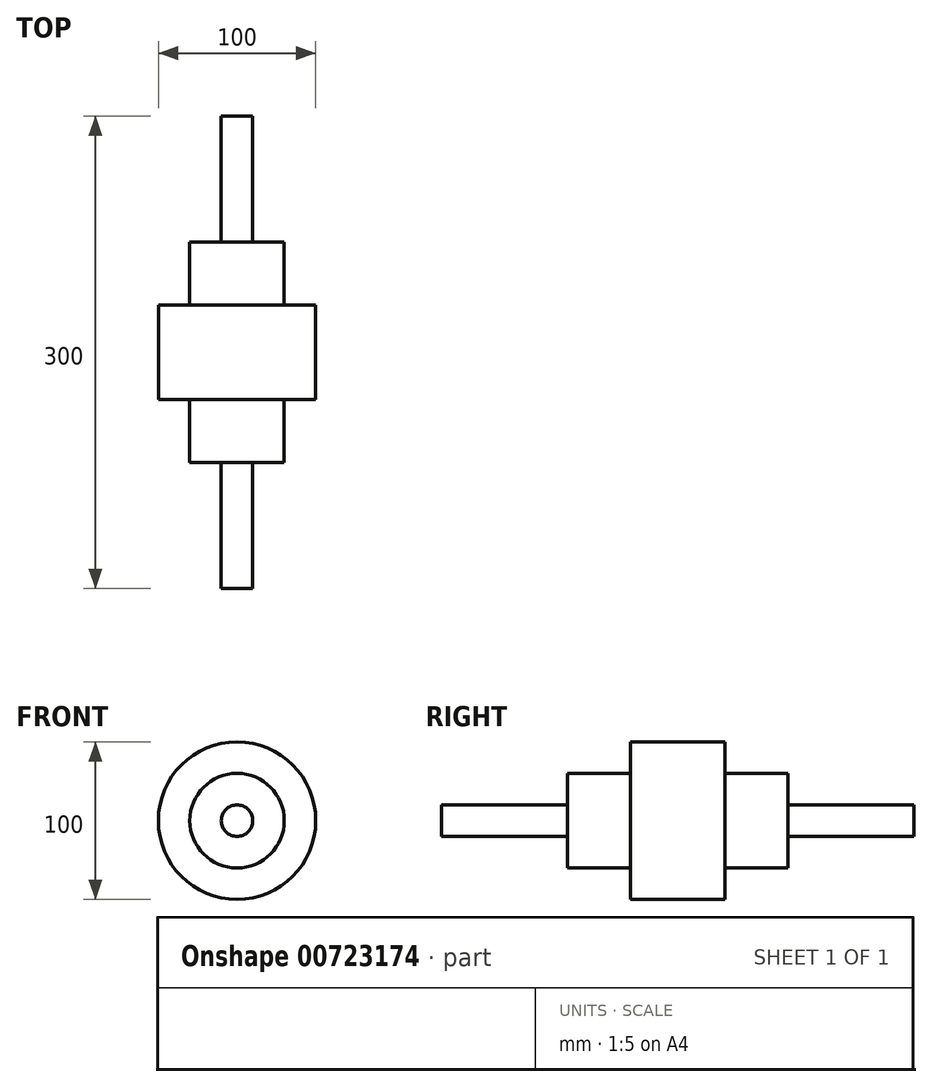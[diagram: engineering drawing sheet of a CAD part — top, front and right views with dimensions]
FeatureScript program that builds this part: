
annotation { "Feature Type Name" : "Feature", "Feature Type Description" : "" }
export const myFeature = defineFeature(function(context is Context, id is Id, definition is map)
    precondition{}
    {
        {
            var Q0;
            Q0=qCreatedBy(makeId("Front.planeOp"),FACE);
            var sketch = newSketch(context, id + "F0", { "sketchPlane" : qUnion([Q0])});
            skCircle(sketch, "E0", {"center": v(0, 0) * mm, "radius": 50 * mm});
            skSolve(sketch);
        }
        {
            var Q0;
            Q0 = qSketchRegion(id + "F0", true);
            extrude(context, id + "F1", {"entities" : qUnion([Q0]), "depth" : 60 * mm, "offsetDistance" : 25.4 * mm});
        }
        {
            var Q0;
            Q0=makeQuery(id+"F1.opExtrude","CAP_FACE",FACE,{"disambiguationData":[OSD([sQuery(id+"F0.wireOp",EDGE,"E0")])],"isStart":false});
            var sketch = newSketch(context, id + "F2", { "sketchPlane" : qUnion([Q0])});
            skCircle(sketch, "E1", {"center": v(0, 0) * mm, "radius": 30 * mm});
            skSolve(sketch);
        }
        {
            var Q0;
            Q0 = qSketchRegion(id + "F2", true);
            extrude(context, id + "F3", {"entities" : qUnion([Q0]), "operationType" : NewBodyOperationType.ADD, "depth" : 40 * mm, "offsetDistance" : 25.4 * mm});
        }
        {
            var Q0;
            Q0=makeQuery(id+"F3.opExtrude","CAP_FACE",FACE,{"disambiguationData":[OSD([sQuery(id+"F2.wireOp",EDGE,"E1")])],"isStart":false});
            var sketch = newSketch(context, id + "F4", { "sketchPlane" : qUnion([Q0])});
            skCircle(sketch, "E2", {"center": v(0, 0) * mm, "radius": 10 * mm});
            skSolve(sketch);
        }
        {
            var Q0;
            Q0 = qSketchRegion(id + "F4", true);
            extrude(context, id + "F5", {"entities" : qUnion([Q0]), "operationType" : NewBodyOperationType.ADD, "depth" : 80 * mm, "offsetDistance" : 25.4 * mm});
        }
        {
            var Q0;
            Q0=makeQuery(id+"F1.opExtrude","CAP_FACE",FACE,{"disambiguationData":[OSD([sQuery(id+"F0.wireOp",EDGE,"E0")])],"isStart":true});
            var sketch = newSketch(context, id + "F6", { "sketchPlane" : qUnion([Q0])});
            skCircle(sketch, "E3", {"center": v(0, 0) * mm, "radius": 30 * mm});
            skSolve(sketch);
        }
        {
            var Q0;
            Q0 = qSketchRegion(id + "F6", true);
            extrude(context, id + "F7", {"entities" : qUnion([Q0]), "operationType" : NewBodyOperationType.ADD, "depth" : 40 * mm, "offsetDistance" : 25.4 * mm});
        }
        {
            var Q0;
            Q0=makeQuery(id+"F7.opExtrude","CAP_FACE",FACE,{"disambiguationData":[OSD([sQuery(id+"F6.wireOp",EDGE,"E3")])],"isStart":false});
            var sketch = newSketch(context, id + "F8", { "sketchPlane" : qUnion([Q0])});
            skCircle(sketch, "E4", {"center": v(0, 0) * mm, "radius": 10 * mm});
            skSolve(sketch);
        }
        {
            var Q0;
            Q0 = qSketchRegion(id + "F8", true);
            extrude(context, id + "F9", {"entities" : qUnion([Q0]), "operationType" : NewBodyOperationType.ADD, "depth" : 80 * mm, "offsetDistance" : 25.4 * mm});
        }
    });
